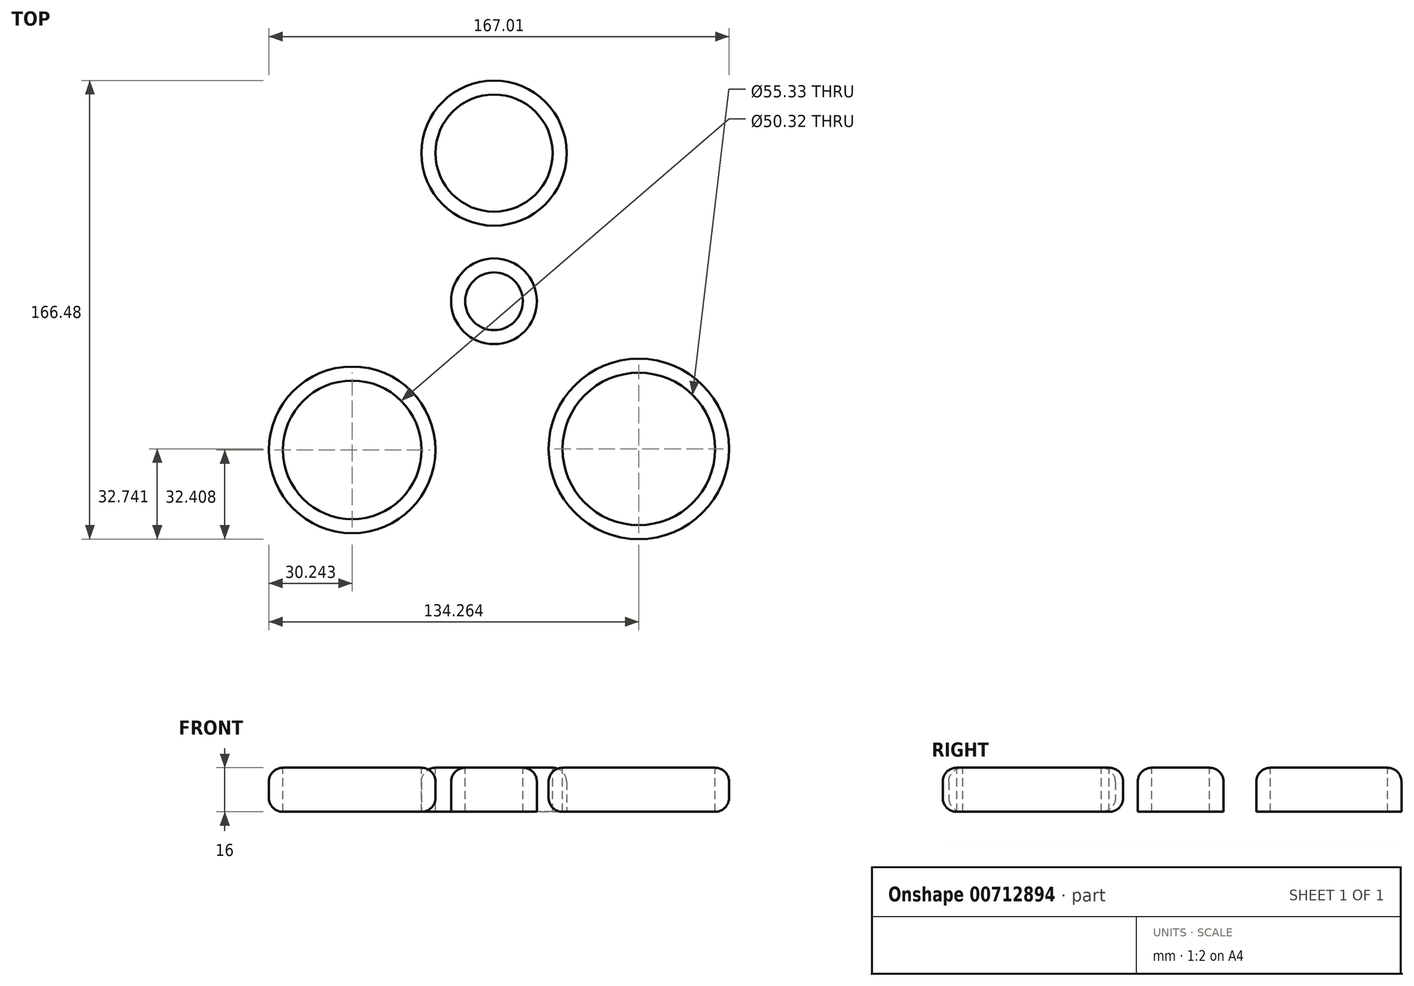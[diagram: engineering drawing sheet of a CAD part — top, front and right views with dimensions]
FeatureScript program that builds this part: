
annotation { "Feature Type Name" : "Feature", "Feature Type Description" : "" }
export const myFeature = defineFeature(function(context is Context, id is Id, definition is map)
    precondition{}
    {
        {
            var Q0;
            Q0=qCreatedBy(makeId("Top.planeOp"),FACE);
            var sketch = newSketch(context, id + "F0", { "sketchPlane" : qUnion([Q0])});
            skCircle(sketch, "E0", {"center": v(0, 0) * mm, "radius": 15.56 * mm});
            skLineSegment(sketch, "E1", {"start": v(0, 0) * mm, "end": v(53.1, -53.44) * mm, "construction": true});
            skLineSegment(sketch, "E2", {"start": v(53.1, -53.44) * mm, "end": v(-52.13, -53.44) * mm, "construction": true});
            skLineSegment(sketch, "E3", {"start": v(-52.13, -53.44) * mm, "end": v(0, 0) * mm, "construction": true});
            skLineSegment(sketch, "E4", {"start": v(0, 54.02) * mm, "end": v(0, 0) * mm, "construction": true});
            skSolve(sketch);
        }
        {
            var Q0;
            Q0=qCreatedBy(makeId("Top.planeOp"),FACE);
            var sketch = newSketch(context, id + "F1", { "sketchPlane" : qUnion([Q0])});
            skCircle(sketch, "E5", {"center": v(0, 53.8) * mm, "radius": 26.34 * mm});
            skCircle(sketch, "E6", {"center": v(-51.48, -53.94) * mm, "radius": 30.24 * mm});
            skCircle(sketch, "E7", {"center": v(52.54, -53.6) * mm, "radius": 32.75 * mm});
            skSolve(sketch);
        }
        {
            var Q0;
            Q0=makeQuery(id+"F1.imprint","IMPRINT",FACE,{"disambiguationData":[TD([[makeQuery(id+"F1.imprint","IMPRINT",EDGE,{"derivedFrom":sQuery(id+"F1.wireOp",EDGE,"E7")}),1.0]])]});
            var Q1;
            Q1=makeQuery(id+"F1.imprint","IMPRINT",FACE,{"disambiguationData":[TD([[makeQuery(id+"F1.imprint","IMPRINT",EDGE,{"derivedFrom":sQuery(id+"F1.wireOp",EDGE,"E6")}),1.0]])]});
            var Q2;
            Q2=makeQuery(id+"F1.imprint","IMPRINT",FACE,{"disambiguationData":[TD([[makeQuery(id+"F1.imprint","IMPRINT",EDGE,{"derivedFrom":sQuery(id+"F1.wireOp",EDGE,"E5")}),1.0]])]});
            var Q3;
            Q3=makeQuery(id+"F0.imprint","IMPRINT",FACE,{"disambiguationData":[TD([[makeQuery(id+"F0.imprint","IMPRINT",EDGE,{"derivedFrom":sQuery(id+"F0.wireOp",EDGE,"E0")}),1.0]])]});
            extrude(context, id + "F2", {"entities" : qUnion([Q0, Q1, Q2, Q3]), "depth" : 16 * mm, "offsetDistance" : 25.4 * mm});
        }
        {
            var Q0;
            Q0=makeQuery(id+"F2.opExtrude","CAP_EDGE",EDGE,{"disambiguationData":[OSD([sQuery(id+"F1.wireOp",EDGE,"E7")])],"isStart":false});
            var Q1;
            Q1=makeQuery(id+"F2.opExtrude","CAP_EDGE",EDGE,{"disambiguationData":[OSD([sQuery(id+"F1.wireOp",EDGE,"E7")])],"isStart":true});
            var Q2;
            Q2=makeQuery(id+"F2.opExtrude","CAP_EDGE",EDGE,{"disambiguationData":[OSD([sQuery(id+"F0.wireOp",EDGE,"E0")])],"isStart":false});
            var Q3;
            Q3=makeQuery(id+"F2.opExtrude","CAP_EDGE",EDGE,{"disambiguationData":[OSD([sQuery(id+"F1.wireOp",EDGE,"E5")])],"isStart":false});
            var Q4;
            Q4=makeQuery(id+"F2.opExtrude","CAP_EDGE",EDGE,{"disambiguationData":[OSD([sQuery(id+"F1.wireOp",EDGE,"E6")])],"isStart":false});
            var Q5;
            Q5=makeQuery(id+"F2.opExtrude","CAP_EDGE",EDGE,{"disambiguationData":[OSD([sQuery(id+"F1.wireOp",EDGE,"E6")])],"isStart":true});
            fillet(context, id + "F3", {"entities" : qUnion([Q0, Q1, Q2, Q3, Q4, Q5]), "radius" : 5.08 * mm, "tangentPropagation" : true, "allowEdgeOverflow" : false});
        }
        {
            var Q0;
            Q0=makeQuery(id+"F2.opExtrude","CAP_FACE",FACE,{"disambiguationData":[OSD([sQuery(id+"F1.wireOp",EDGE,"E6")])],"isStart":false});
            var Q1;
            Q1=makeQuery(id+"F2.opExtrude","CAP_FACE",FACE,{"disambiguationData":[OSD([sQuery(id+"F1.wireOp",EDGE,"E7")])],"isStart":false});
            var Q2;
            Q2=makeQuery(id+"F2.opExtrude","CAP_FACE",FACE,{"disambiguationData":[OSD([sQuery(id+"F0.wireOp",EDGE,"E0")])],"isStart":false});
            var Q3;
            Q3=makeQuery(id+"F2.opExtrude","CAP_FACE",FACE,{"disambiguationData":[OSD([sQuery(id+"F1.wireOp",EDGE,"E5")])],"isStart":false});
            extrude(context, id + "F4", {"entities" : qUnion([Q0, Q1, Q2, Q3]), "operationType" : NewBodyOperationType.REMOVE, "oppositeDirection" : true, "depth" : 25.4 * mm, "offsetDistance" : 25.4 * mm});
        }
    });
